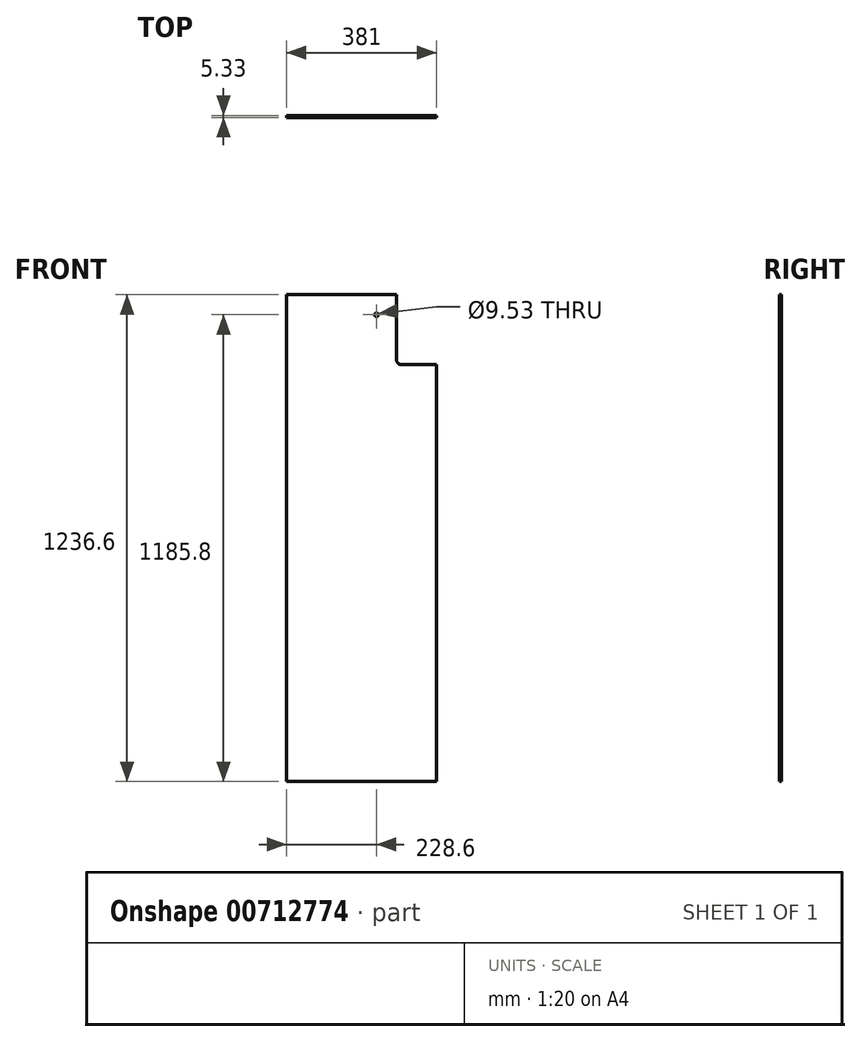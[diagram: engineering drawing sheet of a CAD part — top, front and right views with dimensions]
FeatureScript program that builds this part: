
annotation { "Feature Type Name" : "Feature", "Feature Type Description" : "" }
export const myFeature = defineFeature(function(context is Context, id is Id, definition is map)
    precondition{}
    {
        {
            var Q0;
            Q0=qCreatedBy(makeId("Front.planeOp"),FACE);
            var sketch = newSketch(context, id + "F0", { "sketchPlane" : qUnion([Q0])});
            skLineSegment(sketch, "E0.bottom", {"start": v(-114.3, 0) * mm, "end": v(-495.3, 0) * mm});
            skLineSegment(sketch, "E0.top", {"start": v(-114.3, 1281.05) * mm, "end": v(-495.3, 1281.05) * mm});
            skLineSegment(sketch, "E0.left", {"start": v(-114.3, 0) * mm, "end": v(-114.3, 1281.05) * mm});
            skLineSegment(sketch, "E0.right", {"start": v(-495.3, 0) * mm, "end": v(-495.3, 1281.05) * mm});
            skSolve(sketch);
        }
        {
            var Q0;
            Q0 = qSketchRegion(id + "F0", true);
            extrude(context, id + "F1", {"entities" : qUnion([Q0]), "depth" : 5.33 * mm, "offsetDistance" : 25.4 * mm});
        }
        {
            var Q0;
            Q0=makeQuery(id+"F1.opExtrude","CAP_FACE",FACE,{"disambiguationData":[OSD([sQuery(id+"F0.wireOp",EDGE,"E0.bottom"),sQuery(id+"F0.wireOp",EDGE,"E0.top"),sQuery(id+"F0.wireOp",EDGE,"E0.left"),sQuery(id+"F0.wireOp",EDGE,"E0.right")])],"isStart":false});
            var sketch = newSketch(context, id + "F2", { "sketchPlane" : qUnion([Q0])});
            skLineSegment(sketch, "E1.bottom", {"start": v(-114.3, 1281.05) * mm, "end": v(-215.9, 1281.05) * mm});
            skLineSegment(sketch, "E1.top", {"start": v(-114.3, 1103.25) * mm, "end": v(-203.2, 1103.25) * mm});
            skLineSegment(sketch, "E1.left", {"start": v(-114.3, 1281.05) * mm, "end": v(-114.3, 1103.25) * mm});
            skLineSegment(sketch, "E1.right", {"start": v(-215.9, 1281.05) * mm, "end": v(-215.9, 1115.95) * mm});
            skPoint(sketch, "E2.visualSharp", {"position": v(-215.9, 1103.25) * mm});
            skArc(sketch, "E2.filletArc", {"start": v(-215.9, 1115.95) * mm, "mid": v(-212.18, 1106.97) * mm, "end": v(-203.2, 1103.25) * mm});
            skSolve(sketch);
        }
        {
            var Q0;
            Q0 = qSketchRegion(id + "F2", true);
            extrude(context, id + "F3", {"entities" : qUnion([Q0]), "operationType" : NewBodyOperationType.REMOVE, "oppositeDirection" : true, "depth" : 25.4 * mm, "offsetDistance" : 25.4 * mm});
        }
        {
            var Q0;
            Q0=makeQuery(id+"F1.opExtrude","CAP_FACE",FACE,{"disambiguationData":[OSD([sQuery(id+"F0.wireOp",EDGE,"E0.bottom"),sQuery(id+"F0.wireOp",EDGE,"E0.top"),sQuery(id+"F0.wireOp",EDGE,"E0.left"),sQuery(id+"F0.wireOp",EDGE,"E0.right")])],"isStart":false});
            var sketch = newSketch(context, id + "F4", { "sketchPlane" : qUnion([Q0])});
            skLineSegment(sketch, "E3.bottom", {"start": v(-495.3, 0) * mm, "end": v(-114.3, 0) * mm});
            skLineSegment(sketch, "E3.top", {"start": v(-495.3, 44.45) * mm, "end": v(-114.3, 44.45) * mm});
            skLineSegment(sketch, "E3.left", {"start": v(-495.3, 0) * mm, "end": v(-495.3, 44.45) * mm});
            skLineSegment(sketch, "E3.right", {"start": v(-114.3, 0) * mm, "end": v(-114.3, 44.45) * mm});
            skSolve(sketch);
        }
        {
            var Q0;
            Q0 = qSketchRegion(id + "F4", true);
            extrude(context, id + "F5", {"entities" : qUnion([Q0]), "operationType" : NewBodyOperationType.REMOVE, "oppositeDirection" : true, "depth" : 25.4 * mm, "offsetDistance" : 25.4 * mm});
        }
        {
            var Q0;
            Q0=makeQuery(id+"F1.opExtrude","CAP_FACE",FACE,{"disambiguationData":[OSD([sQuery(id+"F0.wireOp",EDGE,"E0.bottom"),sQuery(id+"F0.wireOp",EDGE,"E0.top"),sQuery(id+"F0.wireOp",EDGE,"E0.left"),sQuery(id+"F0.wireOp",EDGE,"E0.right")])],"isStart":false});
            var sketch = newSketch(context, id + "F6", { "sketchPlane" : qUnion([Q0])});
            skCircle(sketch, "E4", {"center": v(-266.7, 1230.25) * mm, "radius": 4.76 * mm});
            skSolve(sketch);
        }
        {
            var Q0;
            Q0 = qSketchRegion(id + "F6", true);
            extrude(context, id + "F7", {"entities" : qUnion([Q0]), "operationType" : NewBodyOperationType.REMOVE, "oppositeDirection" : true, "depth" : 25.4 * mm, "offsetDistance" : 25.4 * mm});
        }
    });
